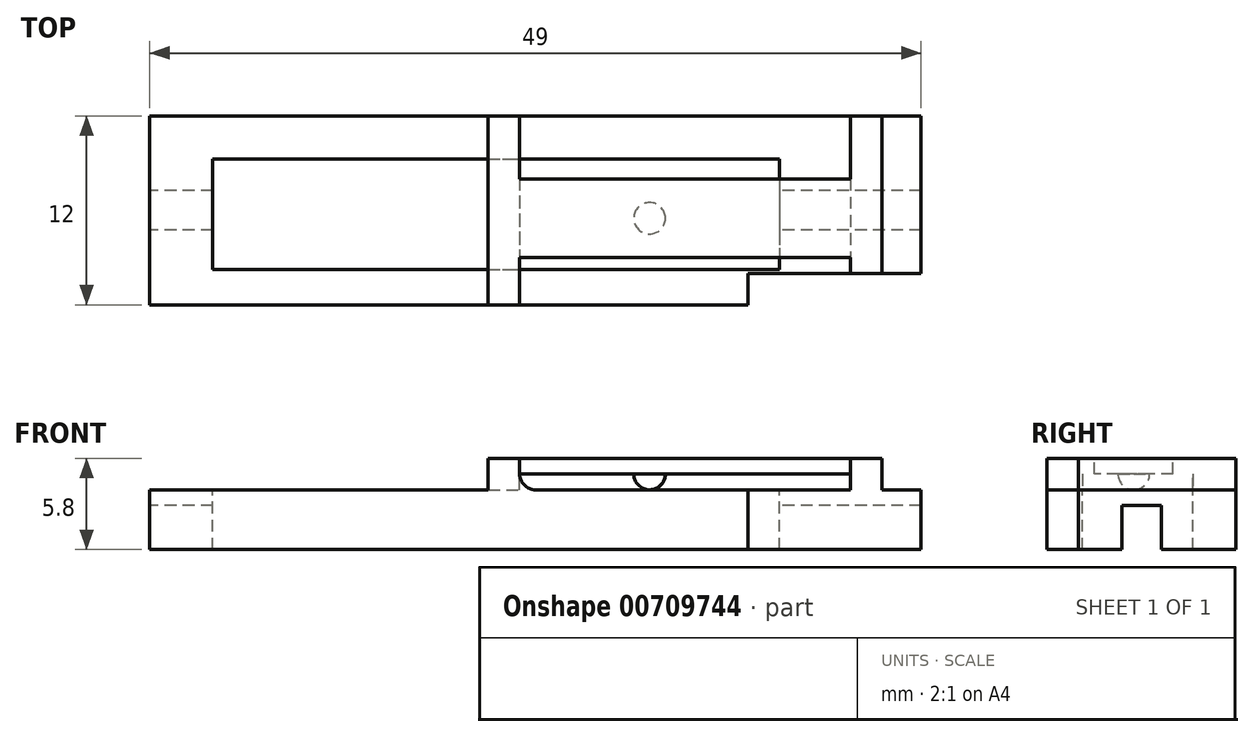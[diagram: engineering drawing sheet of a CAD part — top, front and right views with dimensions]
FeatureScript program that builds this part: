
annotation { "Feature Type Name" : "Feature", "Feature Type Description" : "" }
export const myFeature = defineFeature(function(context is Context, id is Id, definition is map)
    precondition{}
    {
        {
            var Q0;
            Q0=qCreatedBy(makeId("Top.planeOp"),FACE);
            var sketch = newSketch(context, id + "F0", { "sketchPlane" : qUnion([Q0])});
            skLineSegment(sketch, "E0.bottom", {"start": v(0, 0) * mm, "end": v(30, 0) * mm});
            skLineSegment(sketch, "E0.top", {"start": v(0, -12) * mm, "end": v(30, -12) * mm});
            skLineSegment(sketch, "E0.left", {"start": v(0, 0) * mm, "end": v(0, -12) * mm});
            skLineSegment(sketch, "E0.right", {"start": v(30, 0) * mm, "end": v(30, -12) * mm});
            skLineSegment(sketch, "E1.bottom", {"start": v(0, 0) * mm, "end": v(-19, 0) * mm});
            skLineSegment(sketch, "E1.top", {"start": v(0, -12) * mm, "end": v(-19, -12) * mm});
            skLineSegment(sketch, "E1.right", {"start": v(-19, 0) * mm, "end": v(-19, -12) * mm});
            skSolve(sketch);
        }
        {
            var Q0;
            Q0=qSketchRegion(id+"F0",true);
            extrude(context, id + "F1", {"entities" : qUnion([Q0]), "depth" : 3.8 * mm, "offsetDistance" : 25 * mm});
        }
        {
            var Q0;
            Q0=makeQuery(id+"F1.opExtrude","CAP_FACE",FACE,{"disambiguationData":[OSD([sQuery(id+"F0.wireOp",EDGE,"E0.bottom"),sQuery(id+"F0.wireOp",EDGE,"E0.top"),sQuery(id+"F0.wireOp",EDGE,"E0.right"),sQuery(id+"F0.wireOp",EDGE,"E1.bottom"),sQuery(id+"F0.wireOp",EDGE,"E1.top"),sQuery(id+"F0.wireOp",EDGE,"E1.right")])],"isStart":false});
            var sketch = newSketch(context, id + "F2", { "sketchPlane" : qUnion([Q0])});
            skLineSegment(sketch, "E2.bottom", {"start": v(30, -12) * mm, "end": v(19, -12) * mm});
            skLineSegment(sketch, "E2.top", {"start": v(30, -10) * mm, "end": v(19, -10) * mm});
            skLineSegment(sketch, "E2.left", {"start": v(30, -12) * mm, "end": v(30, -10) * mm});
            skLineSegment(sketch, "E2.right", {"start": v(19, -12) * mm, "end": v(19, -10) * mm});
            skLineSegment(sketch, "E3", {"start": v(30, -7.25) * mm, "end": v(-19, -7.25) * mm});
            skLineSegment(sketch, "E4", {"start": v(-13.56, -7.25) * mm, "end": v(-13.56, -12) * mm, "construction": true});
            skLineSegment(sketch, "E5", {"start": v(30, -4.75) * mm, "end": v(-19, -4.75) * mm});
            skLineSegment(sketch, "E6", {"start": v(-13.56, -7.25) * mm, "end": v(-13.56, -4.75) * mm, "construction": true});
            skLineSegment(sketch, "E7.bottom", {"start": v(-15, -2.75) * mm, "end": v(21, -2.75) * mm});
            skLineSegment(sketch, "E7.top", {"start": v(-15, -9.75) * mm, "end": v(21, -9.75) * mm});
            skLineSegment(sketch, "E7.left", {"start": v(-15, -2.75) * mm, "end": v(-15, -9.75) * mm});
            skLineSegment(sketch, "E7.right", {"start": v(21, -2.75) * mm, "end": v(21, -9.75) * mm});
            skLineSegment(sketch, "E8", {"start": v(21, -9.75) * mm, "end": v(30, -9.75) * mm, "construction": true});
            skLineSegment(sketch, "E9", {"start": v(-9.84, -9.75) * mm, "end": v(-9.84, -7.25) * mm, "construction": true});
            skLineSegment(sketch, "E10.bottom", {"start": v(25.5, 0) * mm, "end": v(27.5, 0) * mm});
            skLineSegment(sketch, "E10.top", {"start": v(25.5, -9.75) * mm, "end": v(27.5, -9.75) * mm});
            skLineSegment(sketch, "E10.left", {"start": v(25.5, 0) * mm, "end": v(25.5, -9.75) * mm});
            skLineSegment(sketch, "E10.right", {"start": v(27.5, 0) * mm, "end": v(27.5, -9.75) * mm});
            skLineSegment(sketch, "E11", {"start": v(27.5, -2.06) * mm, "end": v(30, -2.06) * mm, "construction": true});
            skLineSegment(sketch, "E12.bottom", {"start": v(2.5, 0) * mm, "end": v(4.5, 0) * mm});
            skLineSegment(sketch, "E12.top", {"start": v(2.5, -12) * mm, "end": v(4.5, -12) * mm});
            skLineSegment(sketch, "E12.left", {"start": v(2.5, 0) * mm, "end": v(2.5, -12) * mm});
            skLineSegment(sketch, "E12.right", {"start": v(4.5, 0) * mm, "end": v(4.5, -12) * mm});
            skLineSegment(sketch, "E13", {"start": v(2.5, -1.55) * mm, "end": v(27.5, -1.55) * mm, "construction": true});
            skLineSegment(sketch, "E14.top", {"start": v(25.5, -10) * mm, "end": v(27.5, -10) * mm});
            skLineSegment(sketch, "E14.left", {"start": v(25.5, -9.75) * mm, "end": v(25.5, -10) * mm});
            skLineSegment(sketch, "E14.right", {"start": v(27.5, -9.75) * mm, "end": v(27.5, -10) * mm});
            skLineSegment(sketch, "E15", {"start": v(-17.04, -4.75) * mm, "end": v(-17.04, -7.25) * mm});
            skLineSegment(sketch, "E16", {"start": v(-17.04, -6) * mm, "end": v(-17.04, -12) * mm, "construction": true});
            skLineSegment(sketch, "E17", {"start": v(21, -4.45) * mm, "end": v(25.5, -4.45) * mm, "construction": true});
            skLineSegment(sketch, "E18", {"start": v(21, -6.38) * mm, "end": v(15, -6.38) * mm, "construction": true});
            skLineSegment(sketch, "E19", {"start": v(15, -6.38) * mm, "end": v(27.5, -6.38) * mm, "construction": true});
            skLineSegment(sketch, "E20", {"start": v(15, -6.38) * mm, "end": v(2.5, -6.38) * mm, "construction": true});
            skSolve(sketch);
        }
        {
            var Q0;
            {var subQ0=sQuery(id+"F2.wireOp",EDGE,"E3");var subQ1=makeQuery(id+"F1.opExtrude","CAP_EDGE",EDGE,{"disambiguationData":[OSD([sQuery(id+"F0.wireOp",EDGE,"E1.right")])],"isStart":false});var subQ2=makeQuery(id+"F2.imprint","INTERSECT",VERTEX,{"derivedFrom":[subQ1,subQ0]});Q0=makeQuery(id+"F2.imprint","IMPRINT",FACE,{"disambiguationData":[TD([[makeQuery(id+"F2.imprint","IMPRINT",EDGE,{"disambiguationData":[TD([[subQ2,1.0]])],"derivedFrom":subQ0}),-1.0]])]});}
            var Q1;
            {var subQ0=sQuery(id+"F2.wireOp",EDGE,"E12.left");var subQ1=sQuery(id+"F2.wireOp",EDGE,"E5");var subQ2=makeQuery(id+"F2.imprint","INTERSECT",VERTEX,{"derivedFrom":[subQ1,subQ0]});Q1=makeQuery(id+"F2.imprint","IMPRINT",FACE,{"disambiguationData":[TD([[makeQuery(id+"F2.imprint","IMPRINT",EDGE,{"disambiguationData":[TD([[subQ2,-1.0]])],"derivedFrom":subQ1}),-1.0]])]});}
            var Q2;
            {var subQ0=sQuery(id+"F2.wireOp",EDGE,"E12.left");var subQ1=sQuery(id+"F2.wireOp",EDGE,"E3");var subQ2=makeQuery(id+"F2.imprint","INTERSECT",VERTEX,{"derivedFrom":[subQ1,subQ0]});Q2=makeQuery(id+"F2.imprint","IMPRINT",FACE,{"disambiguationData":[TD([[makeQuery(id+"F2.imprint","IMPRINT",EDGE,{"disambiguationData":[TD([[subQ2,-1.0]])],"derivedFrom":subQ1}),-1.0]])]});}
            var Q3;
            {var subQ0=sQuery(id+"F2.wireOp",EDGE,"E12.left");var subQ1=sQuery(id+"F2.wireOp",EDGE,"E3");var subQ2=makeQuery(id+"F2.imprint","INTERSECT",VERTEX,{"derivedFrom":[subQ1,subQ0]});Q3=makeQuery(id+"F2.imprint","IMPRINT",FACE,{"disambiguationData":[TD([[makeQuery(id+"F2.imprint","IMPRINT",EDGE,{"disambiguationData":[TD([[subQ2,-1.0]])],"derivedFrom":subQ1}),1.0]])]});}
            var Q4;
            {var subQ0=sQuery(id+"F2.wireOp",EDGE,"E12.right");var subQ1=sQuery(id+"F2.wireOp",EDGE,"E5");var subQ2=makeQuery(id+"F2.imprint","INTERSECT",VERTEX,{"derivedFrom":[subQ1,subQ0]});Q4=makeQuery(id+"F2.imprint","IMPRINT",FACE,{"disambiguationData":[TD([[makeQuery(id+"F2.imprint","IMPRINT",EDGE,{"disambiguationData":[TD([[subQ2,-1.0]])],"derivedFrom":subQ1}),-1.0]])]});}
            var Q5;
            {var subQ0=sQuery(id+"F2.wireOp",EDGE,"E12.right");var subQ1=sQuery(id+"F2.wireOp",EDGE,"E3");var subQ2=makeQuery(id+"F2.imprint","INTERSECT",VERTEX,{"derivedFrom":[subQ1,subQ0]});Q5=makeQuery(id+"F2.imprint","IMPRINT",FACE,{"disambiguationData":[TD([[makeQuery(id+"F2.imprint","IMPRINT",EDGE,{"disambiguationData":[TD([[subQ2,-1.0]])],"derivedFrom":subQ1}),-1.0]])]});}
            var Q6;
            {var subQ0=sQuery(id+"F2.wireOp",EDGE,"E12.right");var subQ1=sQuery(id+"F2.wireOp",EDGE,"E3");var subQ2=makeQuery(id+"F2.imprint","INTERSECT",VERTEX,{"derivedFrom":[subQ1,subQ0]});Q6=makeQuery(id+"F2.imprint","IMPRINT",FACE,{"disambiguationData":[TD([[makeQuery(id+"F2.imprint","IMPRINT",EDGE,{"disambiguationData":[TD([[subQ2,-1.0]])],"derivedFrom":subQ1}),1.0]])]});}
            var Q7;
            {var subQ0=sQuery(id+"F2.wireOp",EDGE,"E7.right");var subQ1=sQuery(id+"F2.wireOp",EDGE,"E3");var subQ2=makeQuery(id+"F2.imprint","INTERSECT",VERTEX,{"derivedFrom":[subQ1,subQ0]});Q7=makeQuery(id+"F2.imprint","IMPRINT",FACE,{"disambiguationData":[TD([[makeQuery(id+"F2.imprint","IMPRINT",EDGE,{"disambiguationData":[TD([[subQ2,-1.0]])],"derivedFrom":subQ1}),1.0]])]});}
            var Q8;
            {var subQ0=sQuery(id+"F2.wireOp",EDGE,"E7.right");var subQ1=sQuery(id+"F2.wireOp",EDGE,"E3");var subQ2=makeQuery(id+"F2.imprint","INTERSECT",VERTEX,{"derivedFrom":[subQ1,subQ0]});Q8=makeQuery(id+"F2.imprint","IMPRINT",FACE,{"disambiguationData":[TD([[makeQuery(id+"F2.imprint","IMPRINT",EDGE,{"disambiguationData":[TD([[subQ2,-1.0]])],"derivedFrom":subQ1}),-1.0]])]});}
            var Q9;
            {var subQ0=sQuery(id+"F2.wireOp",EDGE,"E7.right");var subQ1=sQuery(id+"F2.wireOp",EDGE,"E5");var subQ2=makeQuery(id+"F2.imprint","INTERSECT",VERTEX,{"derivedFrom":[subQ1,subQ0]});Q9=makeQuery(id+"F2.imprint","IMPRINT",FACE,{"disambiguationData":[TD([[makeQuery(id+"F2.imprint","IMPRINT",EDGE,{"disambiguationData":[TD([[subQ2,-1.0]])],"derivedFrom":subQ1}),-1.0]])]});}
            var Q10;
            {var subQ0=sQuery(id+"F2.wireOp",EDGE,"E10.left");var subQ1=sQuery(id+"F2.wireOp",EDGE,"E3");var subQ2=makeQuery(id+"F2.imprint","INTERSECT",VERTEX,{"derivedFrom":[subQ1,subQ0]});Q10=makeQuery(id+"F2.imprint","IMPRINT",FACE,{"disambiguationData":[TD([[makeQuery(id+"F2.imprint","IMPRINT",EDGE,{"disambiguationData":[TD([[subQ2,-1.0]])],"derivedFrom":subQ1}),-1.0]])]});}
            var Q11;
            {var subQ0=sQuery(id+"F2.wireOp",EDGE,"E10.right");var subQ1=sQuery(id+"F2.wireOp",EDGE,"E3");var subQ2=makeQuery(id+"F2.imprint","INTERSECT",VERTEX,{"derivedFrom":[subQ1,subQ0]});Q11=makeQuery(id+"F2.imprint","IMPRINT",FACE,{"disambiguationData":[TD([[makeQuery(id+"F2.imprint","IMPRINT",EDGE,{"disambiguationData":[TD([[subQ2,-1.0]])],"derivedFrom":subQ1}),-1.0]])]});}
            var Q12;
            {var subQ0=sQuery(id+"F2.wireOp",EDGE,"E3");var subQ1=makeQuery(id+"F1.opExtrude","CAP_EDGE",EDGE,{"disambiguationData":[OSD([sQuery(id+"F0.wireOp",EDGE,"E0.right")])],"isStart":false});var subQ2=makeQuery(id+"F2.imprint","INTERSECT",VERTEX,{"derivedFrom":[subQ1,subQ0]});Q12=makeQuery(id+"F2.imprint","IMPRINT",FACE,{"disambiguationData":[TD([[makeQuery(id+"F2.imprint","IMPRINT",EDGE,{"disambiguationData":[TD([[subQ2,-1.0]])],"derivedFrom":subQ0}),-1.0]])]});}
            var Q13;
            Q13=makeQuery(id+"F2.imprint","IMPRINT",FACE,{"disambiguationData":[TD([[makeQuery(id+"F2.imprint","IMPRINT",EDGE,{"derivedFrom":sQuery(id+"F2.wireOp",EDGE,"E2.bottom")}),1.0]])]});
            var Q14;
            {var subQ0=sQuery(id+"F2.wireOp",EDGE,"E15");Q14=makeQuery(id+"F2.imprint","IMPRINT",FACE,{"disambiguationData":[TD([[makeQuery(id+"F2.imprint","IMPRINT",EDGE,{"derivedFrom":subQ0}),1.0]])]});}
            extrude(context, id + "F3", {"entities" : qUnion([Q0, Q1, Q2, Q3, Q4, Q5, Q6, Q7, Q8, Q9, Q10, Q11, Q12, Q13, Q14]), "operationType" : NewBodyOperationType.REMOVE, "oppositeDirection" : true, "depth" : 25 * mm, "offsetDistance" : 25 * mm});
        }
        {
            var Q0;
            {var subQ0=sQuery(id+"F2.wireOp",EDGE,"E3");var subQ1=makeQuery(id+"F1.opExtrude","CAP_EDGE",EDGE,{"disambiguationData":[OSD([sQuery(id+"F0.wireOp",EDGE,"E1.right")])],"isStart":false});var subQ2=makeQuery(id+"F2.imprint","INTERSECT",VERTEX,{"derivedFrom":[subQ1,subQ0]});Q0=makeQuery(id+"F2.imprint","IMPRINT",FACE,{"disambiguationData":[TD([[makeQuery(id+"F2.imprint","IMPRINT",EDGE,{"disambiguationData":[TD([[subQ2,1.0]])],"derivedFrom":subQ0}),-1.0]])]});}
            var Q1;
            {var subQ0=sQuery(id+"F2.wireOp",EDGE,"E10.left");var subQ1=sQuery(id+"F2.wireOp",EDGE,"E3");var subQ2=makeQuery(id+"F2.imprint","INTERSECT",VERTEX,{"derivedFrom":[subQ1,subQ0]});Q1=makeQuery(id+"F2.imprint","IMPRINT",FACE,{"disambiguationData":[TD([[makeQuery(id+"F2.imprint","IMPRINT",EDGE,{"disambiguationData":[TD([[subQ2,-1.0]])],"derivedFrom":subQ1}),-1.0]])]});}
            var Q2;
            {var subQ0=sQuery(id+"F2.wireOp",EDGE,"E10.right");var subQ1=sQuery(id+"F2.wireOp",EDGE,"E3");var subQ2=makeQuery(id+"F2.imprint","INTERSECT",VERTEX,{"derivedFrom":[subQ1,subQ0]});Q2=makeQuery(id+"F2.imprint","IMPRINT",FACE,{"disambiguationData":[TD([[makeQuery(id+"F2.imprint","IMPRINT",EDGE,{"disambiguationData":[TD([[subQ2,-1.0]])],"derivedFrom":subQ1}),-1.0]])]});}
            var Q3;
            {var subQ0=sQuery(id+"F2.wireOp",EDGE,"E3");var subQ1=makeQuery(id+"F1.opExtrude","CAP_EDGE",EDGE,{"disambiguationData":[OSD([sQuery(id+"F0.wireOp",EDGE,"E0.right")])],"isStart":false});var subQ2=makeQuery(id+"F2.imprint","INTERSECT",VERTEX,{"derivedFrom":[subQ1,subQ0]});Q3=makeQuery(id+"F2.imprint","IMPRINT",FACE,{"disambiguationData":[TD([[makeQuery(id+"F2.imprint","IMPRINT",EDGE,{"disambiguationData":[TD([[subQ2,-1.0]])],"derivedFrom":subQ0}),-1.0]])]});}
            var Q4;
            {var subQ0=sQuery(id+"F2.wireOp",EDGE,"E15");Q4=makeQuery(id+"F2.imprint","IMPRINT",FACE,{"disambiguationData":[TD([[makeQuery(id+"F2.imprint","IMPRINT",EDGE,{"derivedFrom":subQ0}),1.0]])]});}
            extrude(context, id + "F4", {"entities" : qUnion([Q0, Q1, Q2, Q3, Q4]), "operationType" : NewBodyOperationType.ADD, "oppositeDirection" : true, "depth" : 1 * mm, "offsetDistance" : 25 * mm});
        }
        {
            var Q0;
            {var subQ5=sQuery(id+"F2.wireOp",EDGE,"E12.bottom");Q0=makeQuery(id+"F2.imprint","IMPRINT",FACE,{"disambiguationData":[TD([[makeQuery(id+"F2.imprint","IMPRINT",EDGE,{"derivedFrom":subQ5}),-1.0]])]});}
            var Q1;
            {var subQ0=sQuery(id+"F2.wireOp",EDGE,"E12.right");var subQ1=sQuery(id+"F2.wireOp",EDGE,"E5");var subQ2=makeQuery(id+"F2.imprint","INTERSECT",VERTEX,{"derivedFrom":[subQ1,subQ0]});Q1=makeQuery(id+"F2.imprint","IMPRINT",FACE,{"disambiguationData":[TD([[makeQuery(id+"F2.imprint","IMPRINT",EDGE,{"disambiguationData":[TD([[subQ2,-1.0]])],"derivedFrom":subQ1}),-1.0]])]});}
            var Q2;
            {var subQ0=sQuery(id+"F2.wireOp",EDGE,"E12.right");var subQ1=sQuery(id+"F2.wireOp",EDGE,"E3");var subQ2=makeQuery(id+"F2.imprint","INTERSECT",VERTEX,{"derivedFrom":[subQ1,subQ0]});Q2=makeQuery(id+"F2.imprint","IMPRINT",FACE,{"disambiguationData":[TD([[makeQuery(id+"F2.imprint","IMPRINT",EDGE,{"disambiguationData":[TD([[subQ2,-1.0]])],"derivedFrom":subQ1}),-1.0]])]});}
            var Q3;
            {var subQ0=sQuery(id+"F2.wireOp",EDGE,"E12.right");var subQ1=sQuery(id+"F2.wireOp",EDGE,"E3");var subQ2=makeQuery(id+"F2.imprint","INTERSECT",VERTEX,{"derivedFrom":[subQ1,subQ0]});Q3=makeQuery(id+"F2.imprint","IMPRINT",FACE,{"disambiguationData":[TD([[makeQuery(id+"F2.imprint","IMPRINT",EDGE,{"disambiguationData":[TD([[subQ2,-1.0]])],"derivedFrom":subQ1}),1.0]])]});}
            var Q4;
            {var subQ5=sQuery(id+"F2.wireOp",EDGE,"E12.top");Q4=makeQuery(id+"F2.imprint","IMPRINT",FACE,{"disambiguationData":[TD([[makeQuery(id+"F2.imprint","IMPRINT",EDGE,{"derivedFrom":subQ5}),1.0]])]});}
            var Q5;
            {var subQ5=sQuery(id+"F2.wireOp",EDGE,"E10.bottom");Q5=makeQuery(id+"F2.imprint","IMPRINT",FACE,{"disambiguationData":[TD([[makeQuery(id+"F2.imprint","IMPRINT",EDGE,{"derivedFrom":subQ5}),-1.0]])]});}
            var Q6;
            {var subQ0=sQuery(id+"F2.wireOp",EDGE,"E10.right");var subQ1=sQuery(id+"F2.wireOp",EDGE,"E3");var subQ2=makeQuery(id+"F2.imprint","INTERSECT",VERTEX,{"derivedFrom":[subQ1,subQ0]});Q6=makeQuery(id+"F2.imprint","IMPRINT",FACE,{"disambiguationData":[TD([[makeQuery(id+"F2.imprint","IMPRINT",EDGE,{"disambiguationData":[TD([[subQ2,-1.0]])],"derivedFrom":subQ1}),-1.0]])]});}
            var Q7;
            {var subQ5=sQuery(id+"F2.wireOp",EDGE,"E10.top");Q7=makeQuery(id+"F2.imprint","IMPRINT",FACE,{"disambiguationData":[TD([[makeQuery(id+"F2.imprint","IMPRINT",EDGE,{"derivedFrom":subQ5}),1.0]])]});}
            var Q8;
            Q8=makeQuery(id+"F2.imprint","IMPRINT",FACE,{"disambiguationData":[TD([[makeQuery(id+"F2.imprint","IMPRINT",EDGE,{"derivedFrom":sQuery(id+"F2.wireOp",EDGE,"E10.top")}),-1.0]])]});
            extrude(context, id + "F5", {"entities" : qUnion([Q0, Q1, Q2, Q3, Q4, Q5, Q6, Q7, Q8]), "operationType" : NewBodyOperationType.ADD, "depth" : 2 * mm, "offsetDistance" : 25 * mm});
        }
        {
            var Q0;
            Q0=makeQuery(id+"F5.opExtrude","CAP_FACE",FACE,{"disambiguationData":[OSD([sQuery(id+"F2.wireOp",EDGE,"E12.bottom"),sQuery(id+"F2.wireOp",EDGE,"E12.top"),sQuery(id+"F2.wireOp",EDGE,"E12.left"),sQuery(id+"F2.wireOp",EDGE,"E12.right")])],"isStart":false});
            var sketch = newSketch(context, id + "F6", { "sketchPlane" : qUnion([Q0])});
            skLineSegment(sketch, "E21.bottom", {"start": v(4.5, -4) * mm, "end": v(25.5, -4) * mm});
            skLineSegment(sketch, "E21.top", {"start": v(4.5, -9) * mm, "end": v(25.5, -9) * mm});
            skLineSegment(sketch, "E21.left", {"start": v(4.5, -4) * mm, "end": v(4.5, -9) * mm});
            skLineSegment(sketch, "E21.right", {"start": v(25.5, -4) * mm, "end": v(25.5, -9) * mm});
            skLineSegment(sketch, "E22", {"start": v(4.5, -9) * mm, "end": v(4.5, -12) * mm, "construction": true});
            skCircle(sketch, "E23", {"center": v(12.75, -6.5) * mm, "radius": 1 * mm});
            skLineSegment(sketch, "E24", {"start": v(25.5, -6.5) * mm, "end": v(25.5, -4) * mm, "construction": true});
            skLineSegment(sketch, "E25", {"start": v(21, -9) * mm, "end": v(21, -4) * mm, "construction": true});
            skLineSegment(sketch, "E26", {"start": v(25.5, -8.03) * mm, "end": v(21, -8.03) * mm, "construction": true});
            skLineSegment(sketch, "E27", {"start": v(21, -6.5) * mm, "end": v(12.75, -6.5) * mm});
            skLineSegment(sketch, "E28", {"start": v(12.75, -6.5) * mm, "end": v(4.5, -6.5) * mm, "construction": true});
            skSolve(sketch);
        }
        {
            var Q0;
            Q0=makeQuery(id+"F6.imprint","IMPRINT",FACE,{"disambiguationData":[TD([[makeQuery(id+"F6.imprint","IMPRINT",EDGE,{"derivedFrom":sQuery(id+"F6.wireOp",EDGE,"E21.bottom")}),-1.0]])]});
            extrude(context, id + "F7", {"entities" : qUnion([Q0]), "operationType" : NewBodyOperationType.ADD, "oppositeDirection" : true, "depth" : 1 * mm, "offsetDistance" : 25 * mm});
        }
        {
            var Q0;
            Q0=makeQuery(id+"F6.imprint","IMPRINT",FACE,{"disambiguationData":[TD([[makeQuery(id+"F6.imprint","IMPRINT",EDGE,{"derivedFrom":sQuery(id+"F6.wireOp",EDGE,"E23")}),1.0]])]});
            extrude(context, id + "F8", {"entities" : qUnion([Q0]), "operationType" : NewBodyOperationType.ADD, "oppositeDirection" : true, "depth" : 2 * mm, "offsetDistance" : 25 * mm});
        }
        {
            var Q0;
            Q0=makeQuery(id+"F8.opExtrude","CAP_EDGE",EDGE,{"disambiguationData":[OSD([sQuery(id+"F6.wireOp",EDGE,"E23")])],"isStart":false});
            var Q1;
            Q1=makeQuery(id+"F7.opExtrude","CAP_EDGE",EDGE,{"disambiguationData":[OSD([sQuery(id+"F6.wireOp",EDGE,"E21.right")])],"isStart":false});
            var Q2;
            Q2=makeQuery(id+"F7.opExtrude","CAP_EDGE",EDGE,{"disambiguationData":[OSD([sQuery(id+"F6.wireOp",EDGE,"E21.left")])],"isStart":false});
            var Q3;
            {var subQ1=sQuery(id+"F0.wireOp",EDGE,"E1.bottom");var subQ2=sQuery(id+"F0.wireOp",EDGE,"E0.bottom");var subQ3=sQuery(id+"F2.wireOp",EDGE,"E5");var subQ4=sQuery(id+"F2.wireOp",EDGE,"E3");var subQ5=sQuery(id+"F0.wireOp",EDGE,"E1.right");var subQ6=makeQuery(id+"F4.opExtrude","CAP_FACE",FACE,{"disambiguationData":[OSD([subQ5,subQ4,subQ3,sQuery(id+"F2.wireOp",EDGE,"E7.left")])],"isStart":true});var subQ7=sQuery(id+"F0.wireOp",EDGE,"E0.right");var subQ8=makeQuery(id+"F4.opExtrude","CAP_FACE",FACE,{"disambiguationData":[OSD([subQ7,subQ4,subQ3,sQuery(id+"F2.wireOp",EDGE,"E7.right")])],"isStart":true});var subQ9=makeQuery(id+"F1.opExtrude","CAP_FACE",FACE,{"disambiguationData":[OSD([subQ2,sQuery(id+"F0.wireOp",EDGE,"E0.top"),subQ7,subQ1,sQuery(id+"F0.wireOp",EDGE,"E1.top"),subQ5])],"isStart":false});var subQ10=sQuery(id+"F2.wireOp",EDGE,"E12.right");var subQ11=makeQuery(id+"F5.opExtrude","SWEPT_FACE",FACE,{"disambiguationData":[OSD([subQ10])]});Q3=makeQuery(id+"F5.boolean.opBoolean","SPLIT",EDGE,{"disambiguationData":[topologyDisambiguationEdgeConnected([subQ9,subQ8,subQ6,subQ11]),TD([makeQuery(id+"F3.boolean.opBoolean","COPY",FACE,{"derivedFrom":makeQuery(id+"F3.opExtrude","SWEPT_FACE",FACE,{"disambiguationData":[OSD([sQuery(id+"F2.wireOp",EDGE,"E7.bottom")])]})})])],"derivedFrom":makeQuery(id+"F5.opExtrude","CAP_EDGE",EDGE,{"disambiguationData":[OSD([subQ10])],"isStart":true})});}
            var Q4;
            {var subQ0=sQuery(id+"F0.wireOp",EDGE,"E1.top");var subQ1=sQuery(id+"F0.wireOp",EDGE,"E0.top");var subQ3=sQuery(id+"F2.wireOp",EDGE,"E5");var subQ4=sQuery(id+"F2.wireOp",EDGE,"E3");var subQ5=sQuery(id+"F0.wireOp",EDGE,"E0.right");var subQ6=makeQuery(id+"F4.opExtrude","CAP_FACE",FACE,{"disambiguationData":[OSD([subQ5,subQ4,subQ3,sQuery(id+"F2.wireOp",EDGE,"E7.right")])],"isStart":true});var subQ7=sQuery(id+"F0.wireOp",EDGE,"E1.right");var subQ8=makeQuery(id+"F1.opExtrude","CAP_FACE",FACE,{"disambiguationData":[OSD([sQuery(id+"F0.wireOp",EDGE,"E0.bottom"),subQ1,subQ5,sQuery(id+"F0.wireOp",EDGE,"E1.bottom"),subQ0,subQ7])],"isStart":false});var subQ9=sQuery(id+"F2.wireOp",EDGE,"E12.right");var subQ10=makeQuery(id+"F4.opExtrude","CAP_FACE",FACE,{"disambiguationData":[OSD([subQ7,subQ4,subQ3,sQuery(id+"F2.wireOp",EDGE,"E7.left")])],"isStart":true});var subQ11=makeQuery(id+"F5.opExtrude","SWEPT_FACE",FACE,{"disambiguationData":[OSD([subQ9])]});Q4=makeQuery(id+"F5.boolean.opBoolean","SPLIT",EDGE,{"disambiguationData":[topologyDisambiguationEdgeConnected([subQ8,subQ6,subQ10,subQ11]),TD([makeQuery(id+"F3.boolean.opBoolean","COPY",FACE,{"derivedFrom":makeQuery(id+"F3.opExtrude","SWEPT_FACE",FACE,{"disambiguationData":[OSD([sQuery(id+"F2.wireOp",EDGE,"E7.top")])]})})])],"derivedFrom":makeQuery(id+"F5.opExtrude","CAP_EDGE",EDGE,{"disambiguationData":[OSD([subQ9])],"isStart":true})});}
            fillet(context, id + "F9", {"entities" : qUnion([Q0, Q1, Q2, Q3, Q4]), "radius" : 1 * mm, "tangentPropagation" : true, "allowEdgeOverflow" : false});
        }
    });
